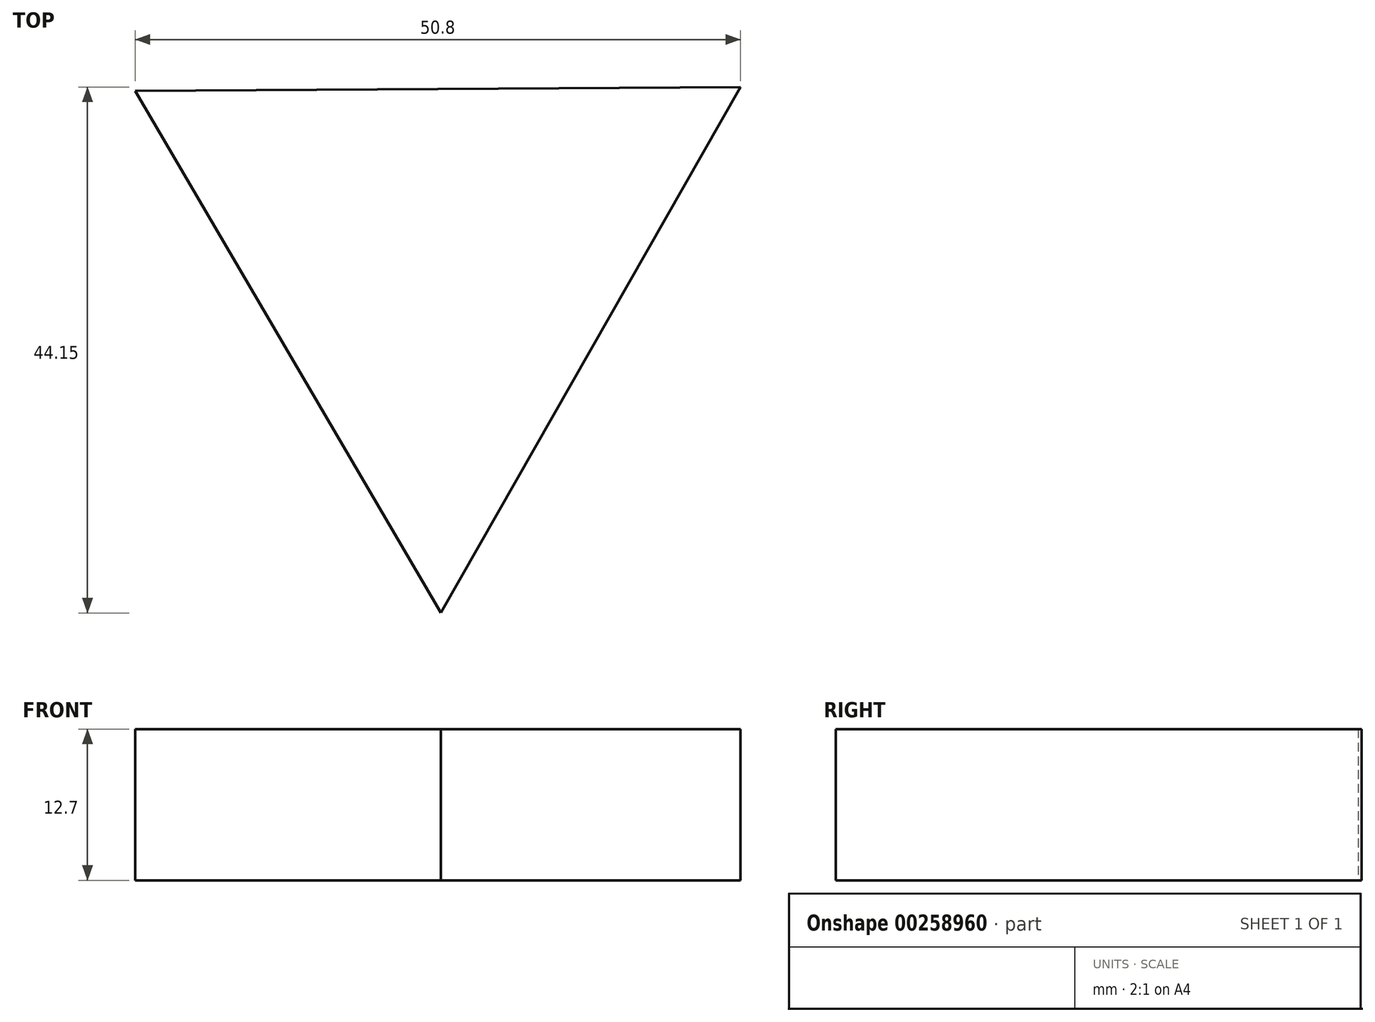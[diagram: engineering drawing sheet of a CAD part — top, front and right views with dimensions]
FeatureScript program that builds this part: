
annotation { "Feature Type Name" : "Feature", "Feature Type Description" : "" }
export const myFeature = defineFeature(function(context is Context, id is Id, definition is map)
    precondition{}
    {
        {
            var Q0;
            Q0=qCreatedBy(makeId("Top.planeOp"),FACE);
            var sketch = newSketch(context, id + "F0", { "sketchPlane" : qUnion([Q0])});
            skCircle(sketch, "E0.cCircle", {"center": v(0, 0) * mm, "radius": 14.66 * mm, "construction": true});
            skLineSegment(sketch, "E0.0", {"start": v(25.31, 14.82) * mm, "end": v(0.18, -29.33) * mm});
            skLineSegment(sketch, "E0.1", {"start": v(0.18, -29.33) * mm, "end": v(-25.49, 14.51) * mm});
            skLineSegment(sketch, "E0.2", {"start": v(-25.49, 14.51) * mm, "end": v(25.31, 14.82) * mm});
            skPoint(sketch, "E0.0.midPoint", {"position": v(12.74, -7.26) * mm});
            skSolve(sketch);
        }
        {
            var Q0;
            Q0=makeQuery(id+"F0.imprint","IMPRINT",FACE,{"disambiguationData":[TD([[makeQuery(id+"F0.imprint","IMPRINT",EDGE,{"derivedFrom":sQuery(id+"F0.wireOp",EDGE,"E0.0")}),-1.0]])]});
            extrude(context, id + "F1", {"entities" : qUnion([Q0]), "depth" : 12.7 * mm});
        }
    });
